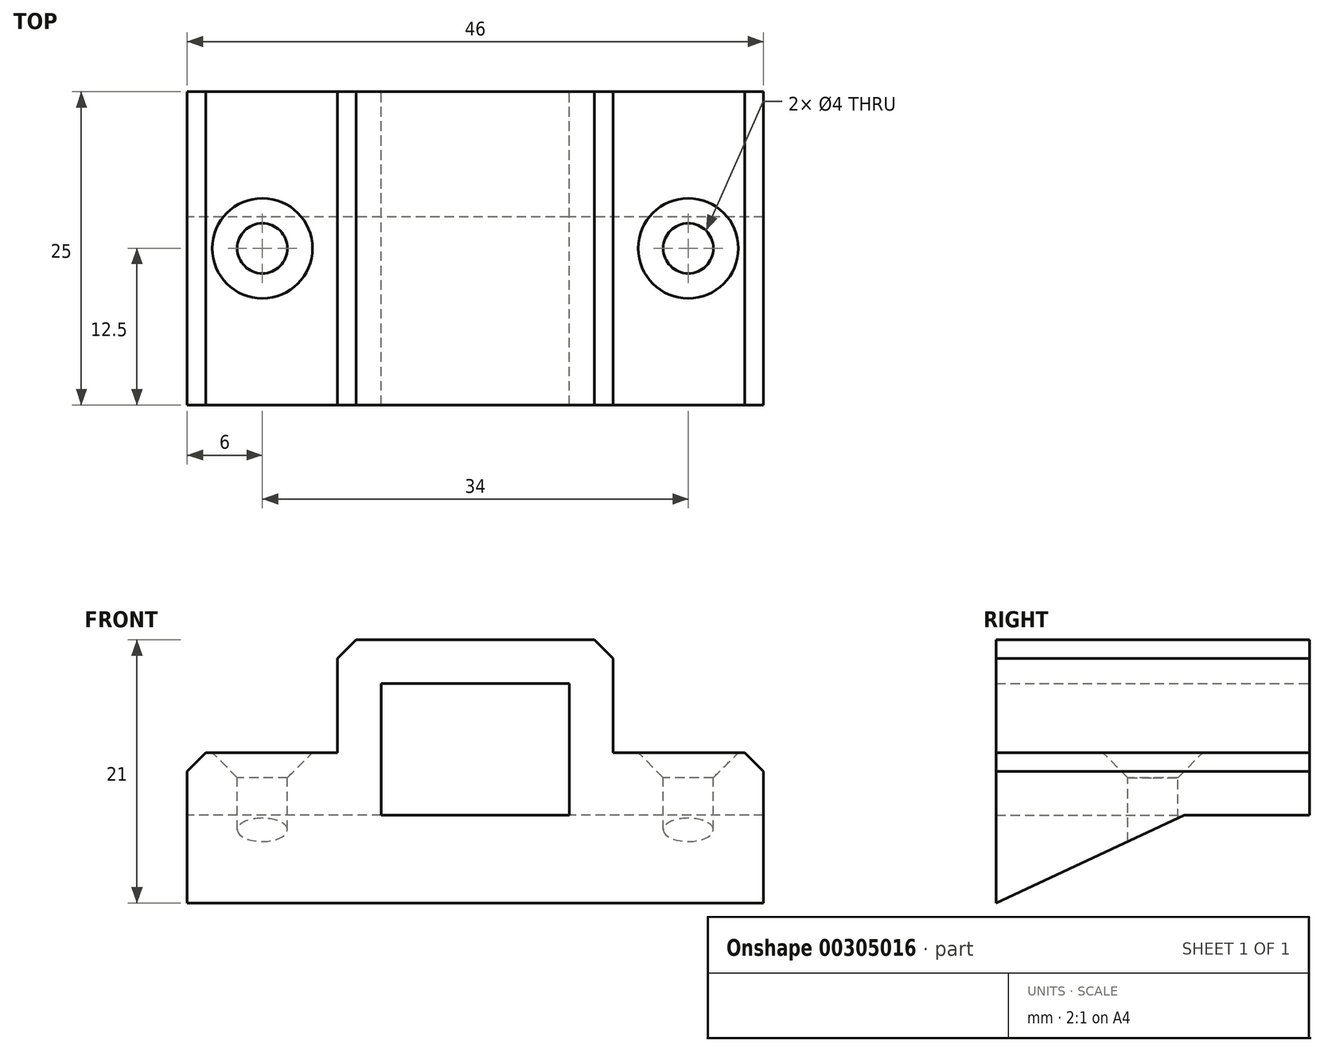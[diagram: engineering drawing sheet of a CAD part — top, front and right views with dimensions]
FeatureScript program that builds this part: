
annotation { "Feature Type Name" : "Feature", "Feature Type Description" : "" }
export const myFeature = defineFeature(function(context is Context, id is Id, definition is map)
    precondition{}
    {
        {
            var Q0;
            Q0=qCreatedBy(makeId("Right.planeOp"),FACE);
            var sketch = newSketch(context, id + "F0", { "sketchPlane" : qUnion([Q0])});
            skLineSegment(sketch, "E0", {"start": v(0, 0) * mm, "end": v(10, 0) * mm});
            skLineSegment(sketch, "E1", {"start": v(10, 0) * mm, "end": v(10, 14) * mm});
            skLineSegment(sketch, "E2", {"start": v(10, 14) * mm, "end": v(-15, 14) * mm});
            skLineSegment(sketch, "E3", {"start": v(-15, 14) * mm, "end": v(-15, -7) * mm});
            skLineSegment(sketch, "E4", {"start": v(-15, -7) * mm, "end": v(0, 0) * mm});
            skSolve(sketch);
        }
        {
            var Q0;
            Q0=makeQuery(id+"F0.imprint","IMPRINT",FACE,{"disambiguationData":[TD([[makeQuery(id+"F0.imprint","IMPRINT",EDGE,{"derivedFrom":sQuery(id+"F0.wireOp",EDGE,"E0")}),1.0]])]});
            extrude(context, id + "F1", {"entities" : qUnion([Q0]), "endBound" : BoundingType.SYMMETRIC, "depth" : 22 * mm});
        }
        {
            var Q0;
            Q0=makeQuery(id+"F1.opExtrude","SWEPT_FACE",FACE,{"disambiguationData":[OSD([sQuery(id+"F0.wireOp",EDGE,"E1")])]});
            var sketch = newSketch(context, id + "F2", { "sketchPlane" : qUnion([Q0])});
            skLineSegment(sketch, "E5.bottom", {"start": v(7.5, 0) * mm, "end": v(-7.5, 0) * mm});
            skLineSegment(sketch, "E5.top", {"start": v(7.5, 10.5) * mm, "end": v(-7.5, 10.5) * mm});
            skLineSegment(sketch, "E5.left", {"start": v(7.5, 0) * mm, "end": v(7.5, 10.5) * mm});
            skLineSegment(sketch, "E5.right", {"start": v(-7.5, 0) * mm, "end": v(-7.5, 10.5) * mm});
            skPoint(sketch, "E5.middle", {"position": v(0, 5.25) * mm});
            skSolve(sketch);
        }
        {
            var Q0;
            Q0=makeQuery(id+"F2.imprint","IMPRINT",FACE,{"disambiguationData":[TD([[makeQuery(id+"F2.imprint","IMPRINT",EDGE,{"derivedFrom":sQuery(id+"F2.wireOp",EDGE,"E5.bottom")}),1.0]])]});
            extrude(context, id + "F3", {"entities" : qUnion([Q0]), "operationType" : NewBodyOperationType.REMOVE, "endBound" : BoundingType.THROUGH_ALL, "oppositeDirection" : true, "depth" : 25 * mm});
        }
        {
            var Q0;
            Q0=makeQuery(id+"F1.opExtrude","CAP_FACE",FACE,{"disambiguationData":[OSD([sQuery(id+"F0.wireOp",EDGE,"E0"),sQuery(id+"F0.wireOp",EDGE,"E1"),sQuery(id+"F0.wireOp",EDGE,"E2"),sQuery(id+"F0.wireOp",EDGE,"E3"),sQuery(id+"F0.wireOp",EDGE,"E4")])],"isStart":true});
            var sketch = newSketch(context, id + "F4", { "sketchPlane" : qUnion([Q0])});
            skLineSegment(sketch, "E6", {"start": v(-10, 5) * mm, "end": v(15, 5) * mm});
            skLineSegment(sketch, "E7", {"start": v(15, 5) * mm, "end": v(15, -7) * mm});
            skLineSegment(sketch, "E8", {"start": v(15, -7) * mm, "end": v(0, 0) * mm});
            skLineSegment(sketch, "E9", {"start": v(0, 0) * mm, "end": v(-10, 0) * mm});
            skLineSegment(sketch, "E10", {"start": v(-10, 0) * mm, "end": v(-10, 5) * mm});
            skSolve(sketch);
        }
        {
            var Q0;
            Q0=makeQuery(id+"F4.imprint","IMPRINT",FACE,{"disambiguationData":[TD([[makeQuery(id+"F4.imprint","IMPRINT",EDGE,{"derivedFrom":sQuery(id+"F4.wireOp",EDGE,"E6")}),-1.0]])]});
            extrude(context, id + "F5", {"entities" : qUnion([Q0]), "operationType" : NewBodyOperationType.ADD, "depth" : 12 * mm});
        }
        {
            var Q0;
            Q0=makeQuery(id+"F1.opExtrude","CAP_FACE",FACE,{"disambiguationData":[OSD([sQuery(id+"F0.wireOp",EDGE,"E0"),sQuery(id+"F0.wireOp",EDGE,"E1"),sQuery(id+"F0.wireOp",EDGE,"E2"),sQuery(id+"F0.wireOp",EDGE,"E3"),sQuery(id+"F0.wireOp",EDGE,"E4")])],"isStart":false});
            var sketch = newSketch(context, id + "F6", { "sketchPlane" : qUnion([Q0])});
            skLineSegment(sketch, "E11", {"start": v(10, 5) * mm, "end": v(10, 0) * mm});
            skLineSegment(sketch, "E12", {"start": v(10, 0) * mm, "end": v(0, 0) * mm});
            skLineSegment(sketch, "E13", {"start": v(0, 0) * mm, "end": v(-15, -7) * mm});
            skLineSegment(sketch, "E14", {"start": v(-15, -7) * mm, "end": v(-15, 5) * mm});
            skLineSegment(sketch, "E15", {"start": v(-15, 5) * mm, "end": v(10, 5) * mm});
            skSolve(sketch);
        }
        {
            var Q0;
            Q0=makeQuery(id+"F6.imprint","IMPRINT",FACE,{"disambiguationData":[TD([[makeQuery(id+"F6.imprint","IMPRINT",EDGE,{"derivedFrom":sQuery(id+"F6.wireOp",EDGE,"E11")}),1.0]])]});
            extrude(context, id + "F7", {"entities" : qUnion([Q0]), "operationType" : NewBodyOperationType.ADD, "depth" : 12 * mm});
        }
        {
            var Q0;
            Q0=makeQuery(id+"F7.opExtrude","CAP_EDGE",EDGE,{"disambiguationData":[OSD([sQuery(id+"F6.wireOp",EDGE,"E15")])],"isStart":true});
            var Q1;
            Q1=makeQuery(id+"F1.opExtrude","CAP_EDGE",EDGE,{"disambiguationData":[OSD([sQuery(id+"F0.wireOp",EDGE,"E2")])],"isStart":false});
            var Q2;
            Q2=makeQuery(id+"F1.opExtrude","CAP_EDGE",EDGE,{"disambiguationData":[OSD([sQuery(id+"F0.wireOp",EDGE,"E2")])],"isStart":true});
            var Q3;
            Q3=makeQuery(id+"F5.opExtrude","CAP_EDGE",EDGE,{"disambiguationData":[OSD([sQuery(id+"F4.wireOp",EDGE,"E6")])],"isStart":true});
            var Q4;
            Q4=makeQuery(id+"F7.opExtrude","CAP_EDGE",EDGE,{"disambiguationData":[OSD([sQuery(id+"F6.wireOp",EDGE,"E15")])],"isStart":false});
            var Q5;
            Q5=makeQuery(id+"F5.opExtrude","CAP_EDGE",EDGE,{"disambiguationData":[OSD([sQuery(id+"F4.wireOp",EDGE,"E6")])],"isStart":false});
            chamfer(context, id + "F8", {"entities" : qUnion([Q0, Q1, Q2, Q3, Q4, Q5]), "width" : 1.5 * mm, "tangentPropagation" : true});
        }
        {
            var Q0;
            Q0=makeQuery(id+"F7.opExtrude","SWEPT_FACE",FACE,{"disambiguationData":[OSD([sQuery(id+"F6.wireOp",EDGE,"E15")])]});
            var sketch = newSketch(context, id + "F9", { "sketchPlane" : qUnion([Q0])});
            skPoint(sketch, "E16", {"position": v(17, -2.5) * mm});
            skPoint(sketch, "E17", {"position": v(-17, -2.5) * mm});
            skPoint(sketch, "E18", {"position": v(17, -15) * mm});
            skLineSegment(sketch, "E19", {"start": v(17, -2.5) * mm, "end": v(0, -2.5) * mm, "construction": true});
            skLineSegment(sketch, "E20", {"start": v(0, -2.5) * mm, "end": v(-17, -2.5) * mm, "construction": true});
            skPoint(sketch, "E21", {"position": v(21.5, -2.5) * mm});
            skSolve(sketch);
        }
        {
            var Q0;
            Q0=sQuery(id+"F9.wireOp",VERTEX,"E20.end");
            var Q1;
            Q1=sQuery(id+"F9.wireOp",VERTEX,"E16");
            var Q2;
            Q2=makeQuery(id+"F1.opExtrude","SWEPT_BODY",BODY,{"disambiguationData":[OSD([sQuery(id+"F0.wireOp",EDGE,"E0"),sQuery(id+"F0.wireOp",EDGE,"E1"),sQuery(id+"F0.wireOp",EDGE,"E2"),sQuery(id+"F0.wireOp",EDGE,"E3"),sQuery(id+"F0.wireOp",EDGE,"E4")])]});
            hole(context, id + "F10", {"style" : HoleStyle.C_SINK, "endStyle" : HoleEndStyle.THROUGH, "holeDiameter" : 4 * mm, "cSinkDiameter" : 8 * mm, "cSinkAngle" : 90 * degree, "tappedDepth" : 12 * mm, "tapClearance" : 3, "locations" : qUnion([Q0, Q1]), "scope" : qUnion([Q2])});
        }
    });
